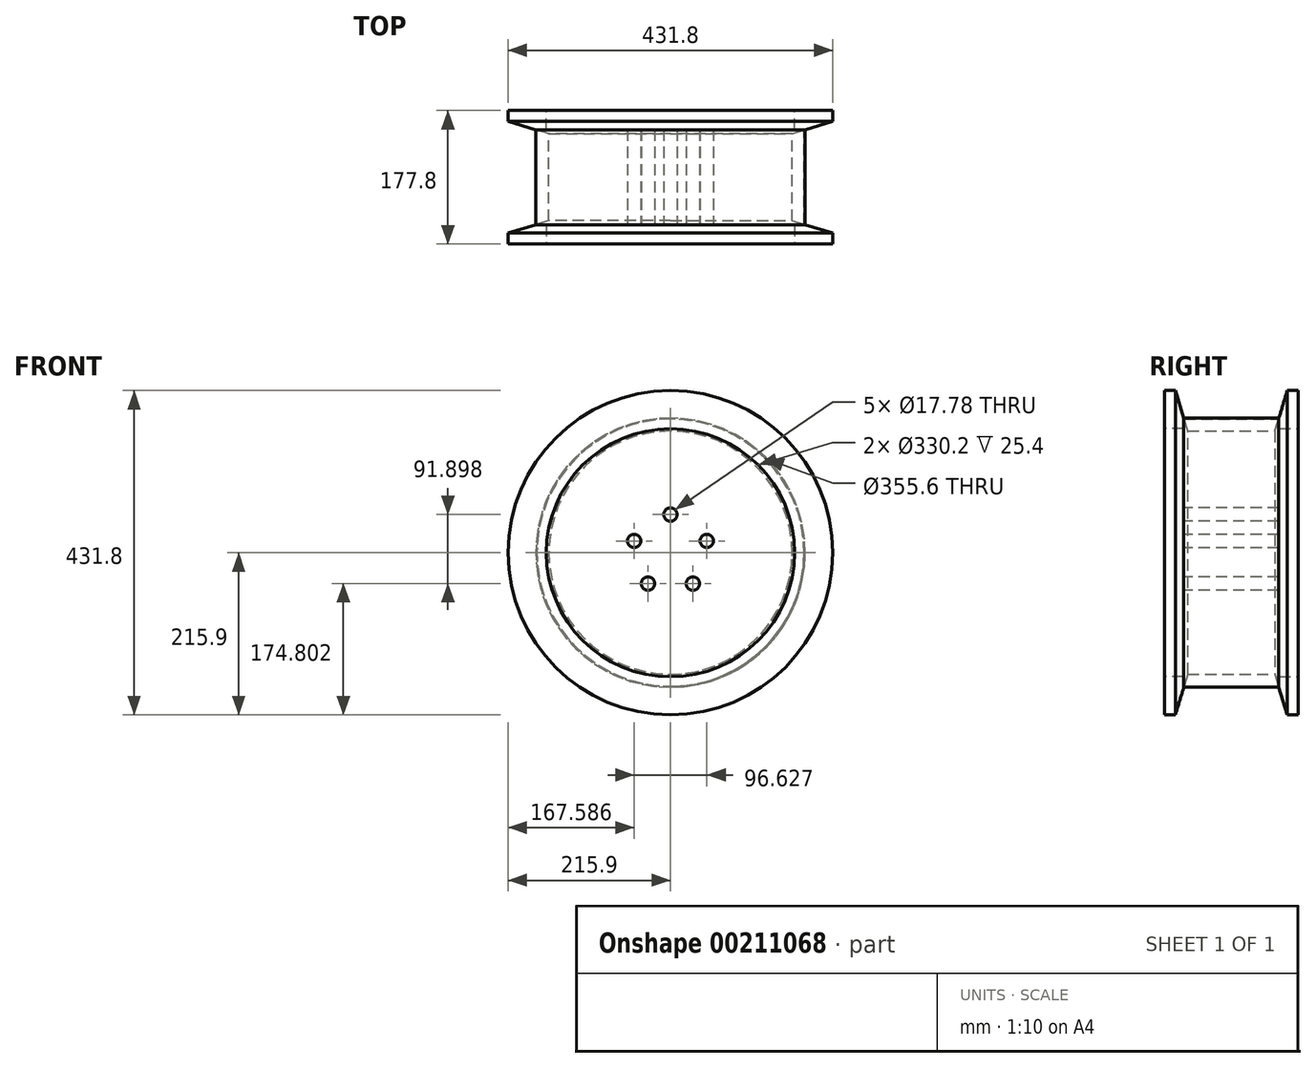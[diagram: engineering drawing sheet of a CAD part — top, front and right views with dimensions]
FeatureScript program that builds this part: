
annotation { "Feature Type Name" : "Feature", "Feature Type Description" : "" }
export const myFeature = defineFeature(function(context is Context, id is Id, definition is map)
    precondition{}
    {
        {
            var Q0;
            Q0=qCreatedBy(makeId("Front.planeOp"),FACE);
            var sketch = newSketch(context, id + "F0", { "sketchPlane" : qUnion([Q0])});
            skCircle(sketch, "E0", {"center": v(0, 0) * mm, "radius": 215.9 * mm});
            skSolve(sketch);
        }
        {
            var Q0;
            Q0=qSketchRegion(id+"F0",true);
            extrude(context, id + "F1", {"entities" : qUnion([Q0]), "oppositeDirection" : true, "depth" : 177.8 * mm});
        }
        {
            var Q0;
            Q0=qCreatedBy(makeId("Right.planeOp"),FACE);
            var sketch = newSketch(context, id + "F2", { "sketchPlane" : qUnion([Q0])});
            skLineSegment(sketch, "E1", {"start": v(12.27, 222.89) * mm, "end": v(30.99, 161.77) * mm});
            skLineSegment(sketch, "E2", {"start": v(30.99, 161.77) * mm, "end": v(85.04, 161.77) * mm});
            skLineSegment(sketch, "E3", {"start": v(88.9, 247.97) * mm, "end": v(88.9, 109.84) * mm});
            skLineSegment(sketch, "E4", {"start": v(85.04, 161.77) * mm, "end": v(88.9, 161.77) * mm});
            skLineSegment(sketch, "E5", {"start": v(12.27, 222.89) * mm, "end": v(88.9, 222.89) * mm});
            skLineSegment(sketch, "E6.MirrorCS", {"start": v(165.53, 222.89) * mm, "end": v(88.9, 222.89) * mm});
            skLineSegment(sketch, "E7.MirrorCS", {"start": v(165.53, 222.89) * mm, "end": v(146.81, 161.77) * mm});
            skLineSegment(sketch, "E8.MirrorCS", {"start": v(146.81, 161.77) * mm, "end": v(92.76, 161.77) * mm});
            skLineSegment(sketch, "E9.MirrorCS", {"start": v(92.76, 161.77) * mm, "end": v(88.9, 161.77) * mm});
            skSolve(sketch);
        }
        {
            var Q0;
            Q0=qCreatedBy(makeId("Right.planeOp"),FACE);
            var sketch = newSketch(context, id + "F3", { "sketchPlane" : qUnion([Q0])});
            skLineSegment(sketch, "E10", {"start": v(0, 0) * mm, "end": v(269.37, 0) * mm});
            skSolve(sketch);
        }
        {
            var Q0;
            {var subQ0=sQuery(id+"F2.wireOp",EDGE,"E6.MirrorCS");Q0=makeQuery(id+"F2.imprint","IMPRINT",FACE,{"disambiguationData":[TD([[makeQuery(id+"F2.imprint","IMPRINT",EDGE,{"derivedFrom":subQ0}),1.0]])]});}
            var Q1;
            Q1=makeQuery(id+"F2.imprint","IMPRINT",FACE,{"disambiguationData":[TD([[makeQuery(id+"F2.imprint","IMPRINT",EDGE,{"derivedFrom":sQuery(id+"F2.wireOp",EDGE,"E1")}),1.0]])]});
            var Q2;
            Q2=sQuery(id+"F3.wireOp",EDGE,"E10");
            revolve(context, id + "F4", {"operationType" : NewBodyOperationType.REMOVE, "entities" : qUnion([Q0, Q1]), "axis" : qUnion([Q2]), "revolveType" : RevolveType.FULL, "oppositeDirection" : true});
        }
        {
            var Q0;
            Q0=makeQuery(id+"F1.opExtrude","CAP_FACE",FACE,{"disambiguationData":[OSD([sQuery(id+"F0.wireOp",EDGE,"E0")])],"isStart":true});
            var sketch = newSketch(context, id + "F5", { "sketchPlane" : qUnion([Q0])});
            skCircle(sketch, "E11", {"center": v(0, 0) * mm, "radius": 165.1 * mm});
            skSolve(sketch);
        }
        {
            var Q0;
            Q0=qSketchRegion(id+"F5",true);
            extrude(context, id + "F6", {"entities" : qUnion([Q0]), "operationType" : NewBodyOperationType.REMOVE, "oppositeDirection" : true, "depth" : 25.4 * mm});
        }
        {
            var Q0;
            Q0=makeQuery(id+"F1.opExtrude","CAP_FACE",FACE,{"disambiguationData":[OSD([sQuery(id+"F0.wireOp",EDGE,"E0")])],"isStart":false});
            var sketch = newSketch(context, id + "F7", { "sketchPlane" : qUnion([Q0])});
            skCircle(sketch, "E12", {"center": v(0, 0) * mm, "radius": 165.1 * mm});
            skSolve(sketch);
        }
        {
            var Q0;
            Q0=qSketchRegion(id+"F7",true);
            extrude(context, id + "F8", {"entities" : qUnion([Q0]), "operationType" : NewBodyOperationType.REMOVE, "oppositeDirection" : true, "depth" : 25.4 * mm});
        }
        {
            var Q0;
            Q0=makeQuery(id+"F6.boolean.opBoolean","COPY",FACE,{"derivedFrom":makeQuery(id+"F6.opExtrude","CAP_FACE",FACE,{"disambiguationData":[OSD([sQuery(id+"F5.wireOp",EDGE,"E11")])],"isStart":false})});
            var sketch = newSketch(context, id + "F9", { "sketchPlane" : qUnion([Q0])});
            skCircle(sketch, "E13", {"center": v(0, 50.8) * mm, "radius": 8.9 * mm});
            skCircle(sketch, "E14.1.0", {"center": v(-48.31, 15.7) * mm, "radius": 8.9 * mm});
            skCircle(sketch, "E14.2.0", {"center": v(-29.86, -41.1) * mm, "radius": 8.9 * mm});
            skCircle(sketch, "E14.3.0", {"center": v(29.86, -41.1) * mm, "radius": 8.9 * mm});
            skCircle(sketch, "E14.4.0", {"center": v(48.31, 15.7) * mm, "radius": 8.9 * mm});
            skPoint(sketch, "E14.center", {"position": v(0, 0) * mm});
            skSolve(sketch);
        }
        {
            var Q0;
            Q0=qSketchRegion(id+"F9",true);
            extrude(context, id + "F10", {"entities" : qUnion([Q0]), "operationType" : NewBodyOperationType.REMOVE, "endBound" : BoundingType.THROUGH_ALL, "oppositeDirection" : true, "depth" : 25.4 * mm});
        }
        {
            var Q0;
            Q0=makeQuery(id+"F1.opExtrude","CAP_FACE",FACE,{"disambiguationData":[OSD([sQuery(id+"F0.wireOp",EDGE,"E0")])],"isStart":false});
            var sketch = newSketch(context, id + "F11", { "sketchPlane" : qUnion([Q0])});
            skCircle(sketch, "E15", {"center": v(0, 0) * mm, "radius": 177.8 * mm});
            skCircle(sketch, "E16", {"center": v(0, 0) * mm, "radius": 179.07 * mm});
            skSolve(sketch);
        }
        {
            var Q0;
            Q0=qSketchRegion(id+"F11",true);
            extrude(context, id + "F12", {"entities" : qUnion([Q0]), "operationType" : NewBodyOperationType.ADD, "oppositeDirection" : true, "depth" : 158.75 * mm});
        }
    });
